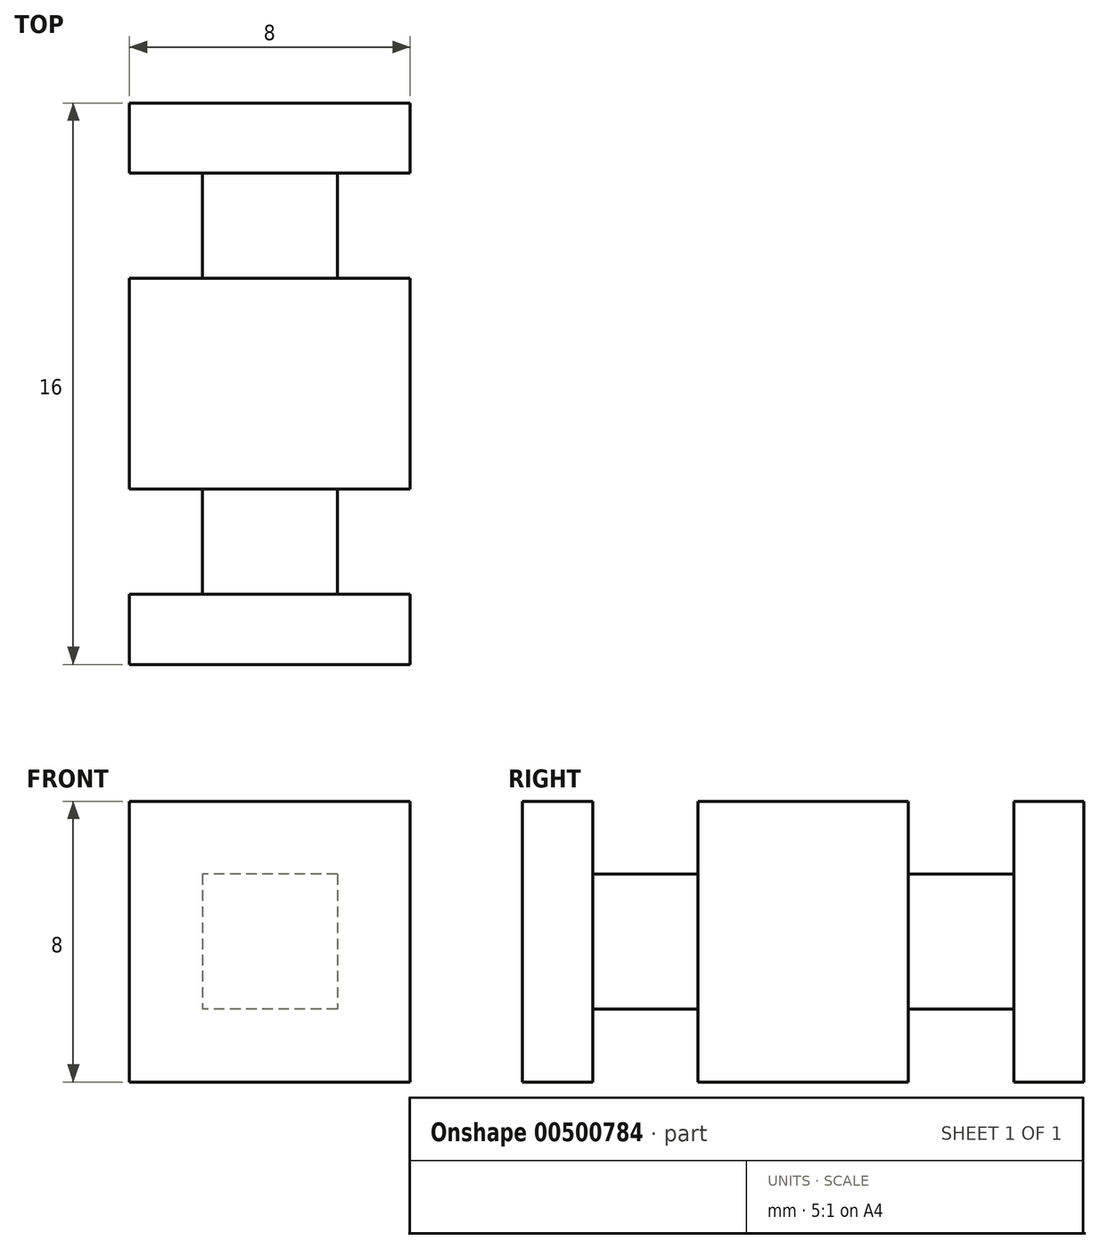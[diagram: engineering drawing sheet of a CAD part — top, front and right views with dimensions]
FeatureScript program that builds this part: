
annotation { "Feature Type Name" : "Feature", "Feature Type Description" : "" }
export const myFeature = defineFeature(function(context is Context, id is Id, definition is map)
    precondition{}
    {
        {
            var Q0;
            Q0=qCreatedBy(makeId("Top.planeOp"),FACE);
            var sketch = newSketch(context, id + "F0", { "sketchPlane" : qUnion([Q0])});
            skLineSegment(sketch, "E0.bottom", {"start": v(4, 3) * mm, "end": v(-4, 3) * mm});
            skLineSegment(sketch, "E0.top", {"start": v(4, -3) * mm, "end": v(-4, -3) * mm});
            skLineSegment(sketch, "E0.left", {"start": v(4, 3) * mm, "end": v(4, -3) * mm});
            skLineSegment(sketch, "E0.right", {"start": v(-4, 3) * mm, "end": v(-4, -3) * mm});
            skPoint(sketch, "E0.middle", {"position": v(0, 0) * mm});
            skSolve(sketch);
        }
        {
            var Q0;
            Q0=makeQuery(id+"F0.imprint","IMPRINT",FACE,{"disambiguationData":[TD([[makeQuery(id+"F0.imprint","IMPRINT",EDGE,{"derivedFrom":sQuery(id+"F0.wireOp",EDGE,"E0.bottom")}),1.0]])]});
            extrude(context, id + "F1", {"entities" : qUnion([Q0]), "depth" : 8 * mm});
        }
        {
            var Q0;
            Q0=makeQuery(id+"F1.opExtrude","SWEPT_FACE",FACE,{"disambiguationData":[OSD([sQuery(id+"F0.wireOp",EDGE,"E0.top")])]});
            var sketch = newSketch(context, id + "F2", { "sketchPlane" : qUnion([Q0])});
            skLineSegment(sketch, "E1.bottom", {"start": v(1.93, 5.93) * mm, "end": v(-1.93, 5.93) * mm});
            skLineSegment(sketch, "E1.top", {"start": v(1.93, 2.08) * mm, "end": v(-1.92, 2.08) * mm});
            skLineSegment(sketch, "E1.left", {"start": v(1.93, 5.93) * mm, "end": v(1.93, 2.08) * mm});
            skLineSegment(sketch, "E1.right", {"start": v(-1.93, 5.93) * mm, "end": v(-1.92, 2.08) * mm});
            skPoint(sketch, "E1.middle", {"position": v(0, 4) * mm});
            skSolve(sketch);
        }
        {
            var Q0;
            Q0=qSketchRegion(id+"F2",true);
            extrude(context, id + "F3", {"entities" : qUnion([Q0]), "operationType" : NewBodyOperationType.ADD, "depth" : 3 * mm});
        }
        {
            var Q0;
            Q0=makeQuery(id+"F3.opExtrude","CAP_FACE",FACE,{"disambiguationData":[OSD([sQuery(id+"F2.wireOp",EDGE,"E1.bottom"),sQuery(id+"F2.wireOp",EDGE,"E1.top"),sQuery(id+"F2.wireOp",EDGE,"E1.left"),sQuery(id+"F2.wireOp",EDGE,"E1.right")])],"isStart":false});
            var sketch = newSketch(context, id + "F4", { "sketchPlane" : qUnion([Q0])});
            skLineSegment(sketch, "E2.bottom", {"start": v(4, 8) * mm, "end": v(-4, 8) * mm});
            skLineSegment(sketch, "E2.top", {"start": v(4, 0) * mm, "end": v(-4, 0) * mm});
            skLineSegment(sketch, "E2.left", {"start": v(4, 8) * mm, "end": v(4, 0) * mm});
            skLineSegment(sketch, "E2.right", {"start": v(-4, 8) * mm, "end": v(-4, 0) * mm});
            skPoint(sketch, "E2.middle", {"position": v(0, 4) * mm});
            skPoint(sketch, "E2.middle.positionSnap0", {"position": v(-1.92, 4) * mm});
            skPoint(sketch, "E2.centerSnap0", {"position": v(-1.92, 4) * mm});
            skSolve(sketch);
        }
        {
            var Q0;
            Q0=makeQuery(id+"F4.imprint","IMPRINT",FACE,{"disambiguationData":[TD([[makeQuery(id+"F4.imprint","IMPRINT",EDGE,{"derivedFrom":sQuery(id+"F4.wireOp",EDGE,"E2.bottom")}),1.0]])]});
            var Q1;
            Q1=makeQuery(id+"F4.imprint","IMPRINT",FACE,{"disambiguationData":[TD([[makeQuery(id+"F4.imprint","IMPRINT",EDGE,{"derivedFrom":makeQuery(id+"F3.opExtrude","CAP_EDGE",EDGE,{"disambiguationData":[OSD([sQuery(id+"F2.wireOp",EDGE,"E1.bottom")])],"isStart":false})}),1.0]])]});
            extrude(context, id + "F5", {"entities" : qUnion([Q0, Q1]), "operationType" : NewBodyOperationType.ADD, "depth" : 2 * mm});
        }
        {
            var Q0;
            Q0=makeQuery(id+"F1.opExtrude","SWEPT_FACE",FACE,{"disambiguationData":[OSD([sQuery(id+"F0.wireOp",EDGE,"E0.bottom")])]});
            var sketch = newSketch(context, id + "F6", { "sketchPlane" : qUnion([Q0])});
            skLineSegment(sketch, "E3.bottom", {"start": v(1.93, 5.92) * mm, "end": v(-1.93, 5.92) * mm});
            skLineSegment(sketch, "E3.top", {"start": v(1.93, 2.07) * mm, "end": v(-1.92, 2.07) * mm});
            skLineSegment(sketch, "E3.left", {"start": v(1.93, 5.92) * mm, "end": v(1.93, 2.07) * mm});
            skLineSegment(sketch, "E3.right", {"start": v(-1.93, 5.92) * mm, "end": v(-1.92, 2.07) * mm});
            skPoint(sketch, "E3.middle", {"position": v(0, 4) * mm});
            skPoint(sketch, "E3.middle.positionSnap0", {"position": v(4, 4) * mm});
            skPoint(sketch, "E3.centerSnap0", {"position": v(4, 4) * mm});
            skSolve(sketch);
        }
        {
            var Q0;
            Q0=makeQuery(id+"F6.imprint","IMPRINT",FACE,{"disambiguationData":[TD([[makeQuery(id+"F6.imprint","IMPRINT",EDGE,{"derivedFrom":sQuery(id+"F6.wireOp",EDGE,"E3.bottom")}),1.0]])]});
            var sketch = newSketch(context, id + "F7", { "sketchPlane" : qUnion([Q0])});
            skSolve(sketch);
        }
        {
            var Q0;
            Q0=makeQuery(id+"F7.imprint","IMPRINT",FACE,{"disambiguationData":[TD([[makeQuery(id+"F7.imprint","IMPRINT",EDGE,{"derivedFrom":makeQuery(id+"F6.imprint","IMPRINT",EDGE,{"derivedFrom":sQuery(id+"F6.wireOp",EDGE,"E3.bottom")})}),1.0]])]});
            extrude(context, id + "F8", {"entities" : qUnion([Q0]), "operationType" : NewBodyOperationType.ADD, "depth" : 3 * mm});
        }
        {
            var Q0;
            Q0=makeQuery(id+"F8.opExtrude","CAP_FACE",FACE,{"disambiguationData":[OSD([sQuery(id+"F6.wireOp",EDGE,"E3.bottom"),sQuery(id+"F6.wireOp",EDGE,"E3.top"),sQuery(id+"F6.wireOp",EDGE,"E3.left"),sQuery(id+"F6.wireOp",EDGE,"E3.right")])],"isStart":false});
            var sketch = newSketch(context, id + "F9", { "sketchPlane" : qUnion([Q0])});
            skLineSegment(sketch, "E4.bottom", {"start": v(4, 8) * mm, "end": v(-4, 8) * mm});
            skLineSegment(sketch, "E4.top", {"start": v(4, 0) * mm, "end": v(-4, 0) * mm});
            skLineSegment(sketch, "E4.left", {"start": v(4, 8) * mm, "end": v(4, 0) * mm});
            skLineSegment(sketch, "E4.right", {"start": v(-4, 8) * mm, "end": v(-4, 0) * mm});
            skPoint(sketch, "E4.middle", {"position": v(0, 4) * mm});
            skPoint(sketch, "E4.middle.positionSnap0", {"position": v(1.93, 4) * mm});
            skPoint(sketch, "E4.centerSnap0", {"position": v(1.93, 4) * mm});
            skSolve(sketch);
        }
        {
            var Q0;
            Q0=makeQuery(id+"F9.imprint","IMPRINT",FACE,{"disambiguationData":[TD([[makeQuery(id+"F9.imprint","IMPRINT",EDGE,{"derivedFrom":sQuery(id+"F9.wireOp",EDGE,"E4.bottom")}),1.0]])]});
            var Q1;
            Q1=makeQuery(id+"F9.imprint","IMPRINT",FACE,{"disambiguationData":[TD([[makeQuery(id+"F9.imprint","IMPRINT",EDGE,{"derivedFrom":makeQuery(id+"F8.opExtrude","CAP_EDGE",EDGE,{"disambiguationData":[OSD([sQuery(id+"F6.wireOp",EDGE,"E3.bottom")])],"isStart":false})}),1.0]])]});
            extrude(context, id + "F10", {"entities" : qUnion([Q0, Q1]), "operationType" : NewBodyOperationType.ADD, "depth" : 2.35 * mm});
        }
        {
            var Q0;
            Q0=makeQuery(id+"F10.opExtrude","CAP_FACE",FACE,{"disambiguationData":[OSD([sQuery(id+"F9.wireOp",EDGE,"E4.bottom"),sQuery(id+"F9.wireOp",EDGE,"E4.top"),sQuery(id+"F9.wireOp",EDGE,"E4.left"),sQuery(id+"F9.wireOp",EDGE,"E4.right")])],"isStart":false});
            extrude(context, id + "F11", {"entities" : qUnion([Q0]), "operationType" : NewBodyOperationType.REMOVE, "oppositeDirection" : true, "depth" : .35 * mm});
        }
    });
